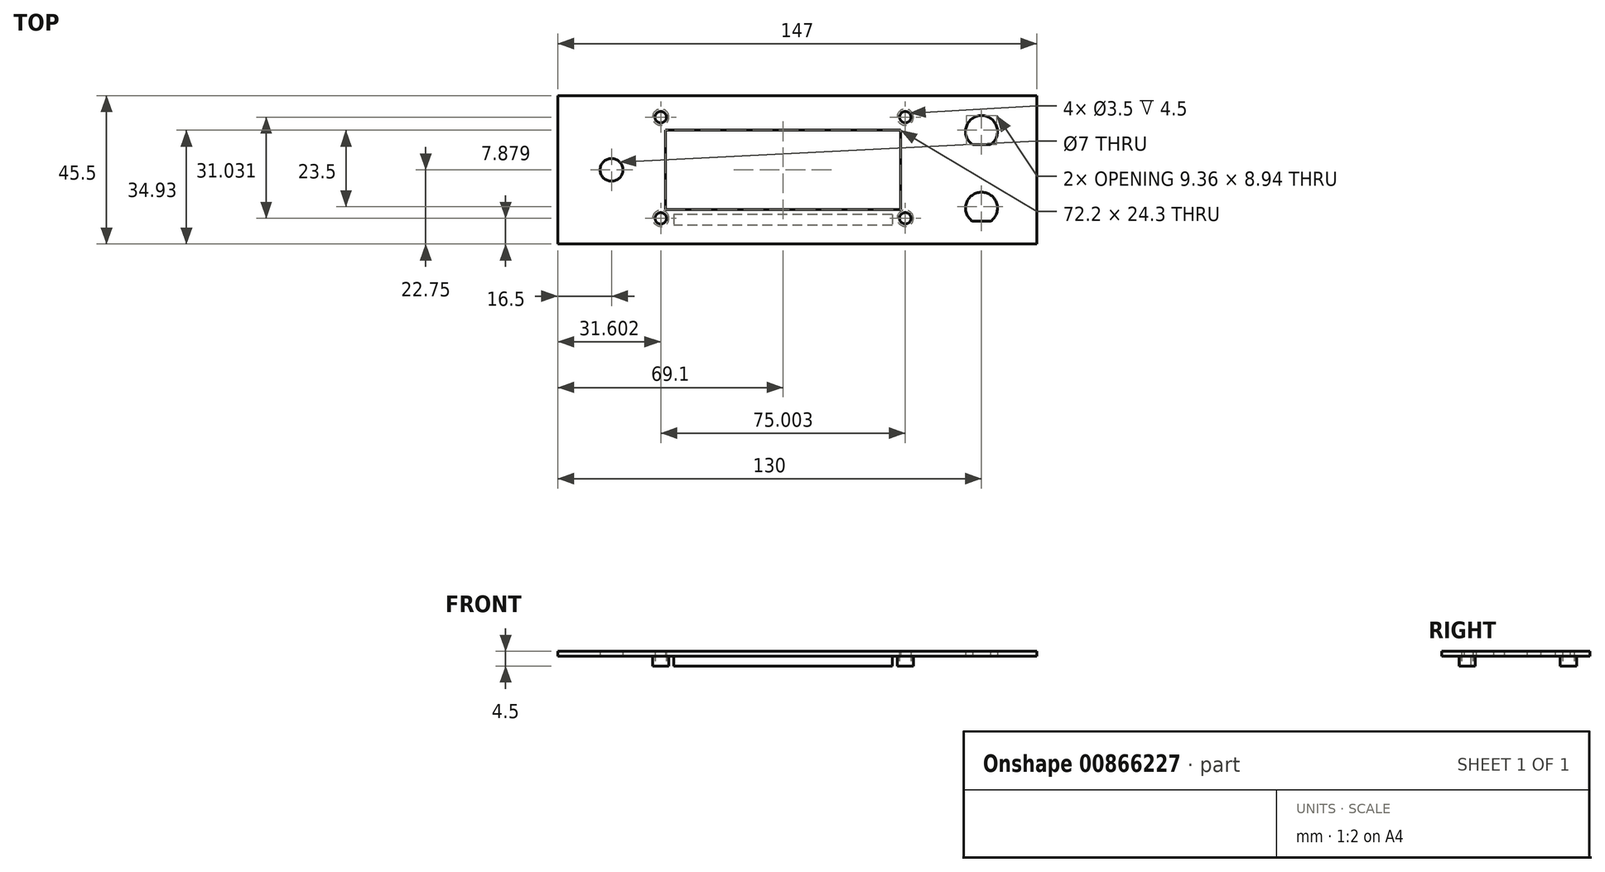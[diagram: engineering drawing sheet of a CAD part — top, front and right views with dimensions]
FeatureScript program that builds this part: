
annotation { "Feature Type Name" : "Feature", "Feature Type Description" : "" }
export const myFeature = defineFeature(function(context is Context, id is Id, definition is map)
    precondition{}
    {
        {
            var Q0;
            Q0=qCreatedBy(makeId("Top.planeOp"),FACE);
            var sketch = newSketch(context, id + "F0", { "sketchPlane" : qUnion([Q0])});
            skLineSegment(sketch, "E0.bottom", {"start": v(73.5, -22.75) * mm, "end": v(-73.5, -22.75) * mm});
            skLineSegment(sketch, "E0.top", {"start": v(73.5, 22.75) * mm, "end": v(-73.5, 22.75) * mm});
            skLineSegment(sketch, "E0.left", {"start": v(73.5, -22.75) * mm, "end": v(73.5, 22.75) * mm});
            skLineSegment(sketch, "E0.right", {"start": v(-73.5, -22.75) * mm, "end": v(-73.5, 22.75) * mm});
            skPoint(sketch, "E0.middle", {"position": v(0, 0) * mm});
            skLineSegment(sketch, "E1.bottom", {"start": v(-40.5, 12.15) * mm, "end": v(31.7, 12.15) * mm});
            skLineSegment(sketch, "E1.top", {"start": v(-40.5, -12.15) * mm, "end": v(31.7, -12.15) * mm});
            skLineSegment(sketch, "E1.left", {"start": v(-40.5, 12.15) * mm, "end": v(-40.5, -12.15) * mm});
            skLineSegment(sketch, "E1.right", {"start": v(31.7, 12.15) * mm, "end": v(31.7, -12.15) * mm});
            skCircle(sketch, "E2", {"center": v(-57, 0) * mm, "radius": 3.5 * mm});
            skPoint(sketch, "E3", {"position": v(-41.9, 16.15) * mm});
            skPoint(sketch, "E4", {"position": v(56.5, 11.75) * mm});
            skArc(sketch, "E5", {"start": v(59.27, 7.71) * mm, "mid": v(56.5, 16.65) * mm, "end": v(53.73, 7.71) * mm});
            skLineSegment(sketch, "E6", {"start": v(53.73, 7.71) * mm, "end": v(59.27, 7.71) * mm});
            skPoint(sketch, "E7", {"position": v(56.5, -11.75) * mm});
            skArc(sketch, "E8", {"start": v(59.27, -15.79) * mm, "mid": v(56.5, -6.85) * mm, "end": v(53.73, -15.79) * mm});
            skLineSegment(sketch, "E9", {"start": v(53.73, -15.79) * mm, "end": v(59.27, -15.79) * mm});
            skPoint(sketch, "E10", {"position": v(33.1, 16.15) * mm});
            skLineSegment(sketch, "E11", {"start": v(-41.9, 16.15) * mm, "end": v(-41.9, -22.75) * mm, "construction": true});
            skLineSegment(sketch, "E12", {"start": v(33.1, 16.15) * mm, "end": v(33.1, -22.75) * mm, "construction": true});
            skPoint(sketch, "E13", {"position": v(-41.9, -14.85) * mm});
            skPoint(sketch, "E14", {"position": v(33.1, -14.85) * mm});
            skLineSegment(sketch, "E15.bottom", {"start": v(29.1, -13.66) * mm, "end": v(-37.9, -13.66) * mm});
            skLineSegment(sketch, "E15.top", {"start": v(29.1, -16.96) * mm, "end": v(-37.9, -16.96) * mm});
            skLineSegment(sketch, "E15.left", {"start": v(29.1, -13.66) * mm, "end": v(29.1, -16.96) * mm});
            skLineSegment(sketch, "E15.right", {"start": v(-37.9, -13.66) * mm, "end": v(-37.9, -16.96) * mm});
            skSolve(sketch);
        }
        {
            var Q0;
            Q0=makeQuery(id+"F0.imprint","IMPRINT",FACE,{"disambiguationData":[TD([[makeQuery(id+"F0.imprint","IMPRINT",EDGE,{"derivedFrom":sQuery(id+"F0.wireOp",EDGE,"E0.bottom")}),-1.0]])]});
            extrude(context, id + "F1", {"entities" : qUnion([Q0]), "depth" : 1.5 * mm, "offsetDistance" : 25 * mm});
        }
        {
            var Q0;
            Q0 = qSketchRegion(id + "F0", true);
            extrude(context, id + "F2", {"entities" : qUnion([Q0]), "operationType" : NewBodyOperationType.ADD, "depth" : 1.5 * mm, "offsetDistance" : 25 * mm});
        }
        {
            var Q0;
            Q0=makeQuery(id+"F0.imprint","IMPRINT",FACE,{"disambiguationData":[TD([[makeQuery(id+"F0.imprint","IMPRINT",EDGE,{"derivedFrom":sQuery(id+"F0.wireOp",EDGE,"E0.bottom")}),-1.0]])]});
            extrude(context, id + "F3", {"entities" : qUnion([Q0]), "operationType" : NewBodyOperationType.ADD, "depth" : 1.5 * mm, "offsetDistance" : 25 * mm});
        }
        {
            var Q0;
            Q0=makeQuery(id+"F0.imprint","IMPRINT",FACE,{"disambiguationData":[TD([[makeQuery(id+"F0.imprint","IMPRINT",EDGE,{"derivedFrom":sQuery(id+"F0.wireOp",EDGE,"E15.bottom")}),1.0]])]});
            extrude(context, id + "F4", {"entities" : qUnion([Q0]), "operationType" : NewBodyOperationType.ADD, "endBound" : BoundingType.SYMMETRIC, "oppositeDirection" : true, "depth" : 3 * mm, "offsetDistance" : 25 * mm});
        }
        {
            var Q0;
            Q0=makeQuery(id+"F4.opExtrude","CAP_FACE",FACE,{"disambiguationData":[OSD([sQuery(id+"F0.wireOp",EDGE,"E15.bottom"),sQuery(id+"F0.wireOp",EDGE,"E15.top"),sQuery(id+"F0.wireOp",EDGE,"E15.left"),sQuery(id+"F0.wireOp",EDGE,"E15.right")])],"isStart":false});
            extrude(context, id + "F5", {"entities" : qUnion([Q0]), "operationType" : NewBodyOperationType.ADD, "depth" : 1.5 * mm, "offsetDistance" : 25 * mm});
        }
        {
            var Q0;
            Q0=makeQuery(id+"F0.imprint","IMPRINT",FACE,{"disambiguationData":[TD([[makeQuery(id+"F0.imprint","IMPRINT",EDGE,{"derivedFrom":sQuery(id+"F0.wireOp",EDGE,"E0.bottom")}),-1.0]])]});
            var sketch = newSketch(context, id + "F6", { "sketchPlane" : qUnion([Q0])});
            skCircle(sketch, "E16", {"center": v(33.1, 16.16) * mm, "radius": 2.5 * mm});
            skSolve(sketch);
        }
        {
            var Q0;
            Q0 = qSketchRegion(id + "F6", true);
            extrude(context, id + "F7", {"entities" : qUnion([Q0]), "operationType" : NewBodyOperationType.ADD, "oppositeDirection" : true, "depth" : 3 * mm, "offsetDistance" : 25 * mm});
        }
        {
            var Q0;
            Q0=makeQuery(id+"F7.opExtrude","CAP_FACE",FACE,{"disambiguationData":[OSD([sQuery(id+"F6.wireOp",EDGE,"E16")])],"isStart":false});
            var sketch = newSketch(context, id + "F8", { "sketchPlane" : qUnion([Q0])});
            skCircle(sketch, "E17", {"center": v(33.1, -16.16) * mm, "radius": 1.75 * mm});
            skSolve(sketch);
        }
        {
            var Q0;
            Q0 = qSketchRegion(id + "F8", true);
            extrude(context, id + "F9", {"entities" : qUnion([Q0]), "operationType" : NewBodyOperationType.REMOVE, "oppositeDirection" : true, "depth" : 6 * mm, "offsetDistance" : 25 * mm});
        }
        {
            var Q0;
            Q0=makeQuery(id+"F0.imprint","IMPRINT",FACE,{"disambiguationData":[TD([[makeQuery(id+"F0.imprint","IMPRINT",EDGE,{"derivedFrom":sQuery(id+"F0.wireOp",EDGE,"E0.bottom")}),-1.0]])]});
            var sketch = newSketch(context, id + "F10", { "sketchPlane" : qUnion([Q0])});
            skCircle(sketch, "E18", {"center": v(-41.9, 16.16) * mm, "radius": 2.5 * mm});
            skSolve(sketch);
        }
        {
            var Q0;
            Q0 = qSketchRegion(id + "F10", true);
            extrude(context, id + "F11", {"entities" : qUnion([Q0]), "operationType" : NewBodyOperationType.ADD, "oppositeDirection" : true, "depth" : 3 * mm, "offsetDistance" : 25 * mm});
        }
        {
            var Q0;
            Q0=makeQuery(id+"F11.opExtrude","CAP_FACE",FACE,{"disambiguationData":[OSD([sQuery(id+"F10.wireOp",EDGE,"E18")])],"isStart":false});
            var sketch = newSketch(context, id + "F12", { "sketchPlane" : qUnion([Q0])});
            skCircle(sketch, "E19", {"center": v(-41.9, -16.16) * mm, "radius": 1.75 * mm});
            skSolve(sketch);
        }
        {
            var Q0;
            Q0 = qSketchRegion(id + "F12", true);
            extrude(context, id + "F13", {"entities" : qUnion([Q0]), "operationType" : NewBodyOperationType.REMOVE, "oppositeDirection" : true, "depth" : 25 * mm, "offsetDistance" : 25 * mm});
        }
        {
            var Q0;
            Q0=makeQuery(id+"F0.imprint","IMPRINT",FACE,{"disambiguationData":[TD([[makeQuery(id+"F0.imprint","IMPRINT",EDGE,{"derivedFrom":sQuery(id+"F0.wireOp",EDGE,"E0.bottom")}),-1.0]])]});
            var sketch = newSketch(context, id + "F14", { "sketchPlane" : qUnion([Q0])});
            skCircle(sketch, "E20", {"center": v(-41.9, -14.87) * mm, "radius": 2.5 * mm});
            skSolve(sketch);
        }
        {
            var Q0;
            Q0 = qSketchRegion(id + "F14", true);
            extrude(context, id + "F15", {"entities" : qUnion([Q0]), "operationType" : NewBodyOperationType.ADD, "oppositeDirection" : true, "depth" : 3 * mm, "offsetDistance" : 25 * mm});
        }
        {
            var Q0;
            Q0=makeQuery(id+"F15.opExtrude","CAP_FACE",FACE,{"disambiguationData":[OSD([sQuery(id+"F14.wireOp",EDGE,"E20")])],"isStart":false});
            var sketch = newSketch(context, id + "F16", { "sketchPlane" : qUnion([Q0])});
            skCircle(sketch, "E21", {"center": v(-41.9, 14.87) * mm, "radius": 1.75 * mm});
            skSolve(sketch);
        }
        {
            var Q0;
            Q0 = qSketchRegion(id + "F16", true);
            extrude(context, id + "F17", {"entities" : qUnion([Q0]), "operationType" : NewBodyOperationType.REMOVE, "oppositeDirection" : true, "depth" : 25 * mm, "offsetDistance" : 25 * mm});
        }
        {
            var Q0;
            Q0=makeQuery(id+"F0.imprint","IMPRINT",FACE,{"disambiguationData":[TD([[makeQuery(id+"F0.imprint","IMPRINT",EDGE,{"derivedFrom":sQuery(id+"F0.wireOp",EDGE,"E0.bottom")}),-1.0]])]});
            var sketch = newSketch(context, id + "F18", { "sketchPlane" : qUnion([Q0])});
            skCircle(sketch, "E22", {"center": v(33.1, -14.86) * mm, "radius": 2.5 * mm});
            skSolve(sketch);
        }
        {
            var Q0;
            Q0 = qSketchRegion(id + "F18", true);
            extrude(context, id + "F19", {"entities" : qUnion([Q0]), "operationType" : NewBodyOperationType.ADD, "oppositeDirection" : true, "depth" : 3 * mm, "offsetDistance" : 25 * mm});
        }
        {
            var Q0;
            Q0=makeQuery(id+"F19.opExtrude","CAP_FACE",FACE,{"disambiguationData":[OSD([sQuery(id+"F18.wireOp",EDGE,"E22")])],"isStart":false});
            var sketch = newSketch(context, id + "F20", { "sketchPlane" : qUnion([Q0])});
            skCircle(sketch, "E23", {"center": v(33.1, 14.86) * mm, "radius": 1.75 * mm});
            skSolve(sketch);
        }
        {
            var Q0;
            Q0 = qSketchRegion(id + "F20", true);
            extrude(context, id + "F21", {"entities" : qUnion([Q0]), "operationType" : NewBodyOperationType.REMOVE, "oppositeDirection" : true, "depth" : 25 * mm, "offsetDistance" : 25 * mm});
        }
    });
